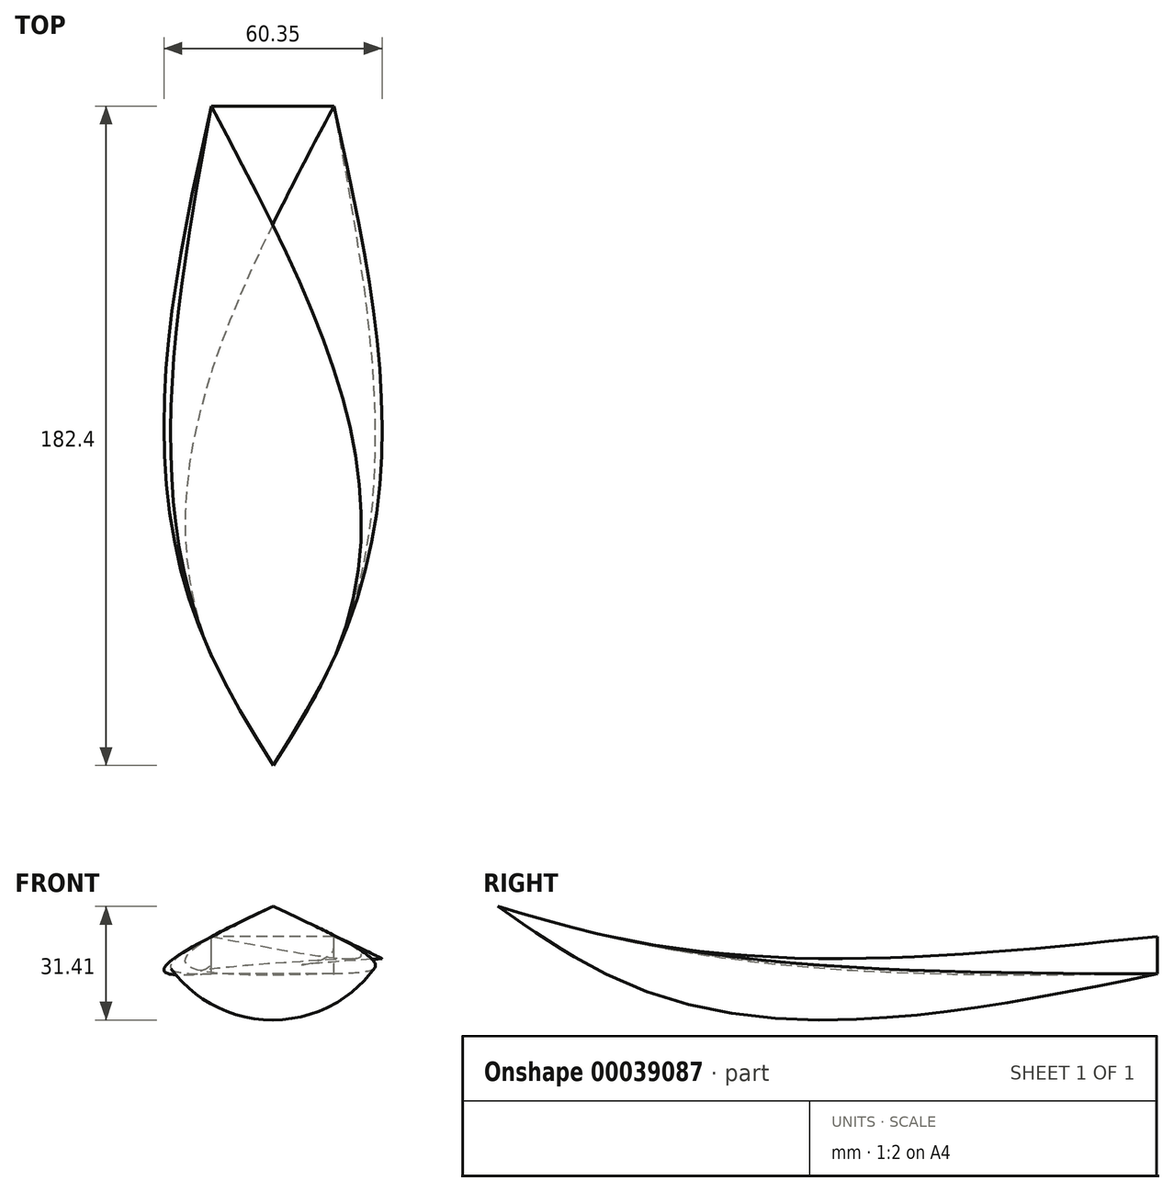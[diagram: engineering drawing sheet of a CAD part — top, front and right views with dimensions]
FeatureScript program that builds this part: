
annotation { "Feature Type Name" : "Feature", "Feature Type Description" : "" }
export const myFeature = defineFeature(function(context is Context, id is Id, definition is map)
    precondition{}
    {
        {
            var Q0;
            Q0=qCreatedBy(makeId("Front.planeOp"),FACE);
            var sketch = newSketch(context, id + "F0", { "sketchPlane" : qUnion([Q0])});
            skLineSegment(sketch, "E0.bottom", {"start": v(46.82, 0) * mm, "end": v(12.91, 0) * mm});
            skLineSegment(sketch, "E0.top", {"start": v(46.82, 10.4) * mm, "end": v(12.91, 10.4) * mm});
            skLineSegment(sketch, "E0.left", {"start": v(46.82, 0) * mm, "end": v(46.82, 10.4) * mm});
            skLineSegment(sketch, "E0.right", {"start": v(12.91, 0) * mm, "end": v(12.91, 10.4) * mm});
            skLineSegment(sketch, "E1.MirrorCS", {"start": v(-12.91, 0) * mm, "end": v(-12.91, 10.4) * mm});
            skLineSegment(sketch, "E2.MirrorCS", {"start": v(-46.82, 0) * mm, "end": v(-46.82, 10.4) * mm});
            skLineSegment(sketch, "E3.MirrorCS", {"start": v(-46.82, 0) * mm, "end": v(-12.91, 0) * mm});
            skLineSegment(sketch, "E4.MirrorCS", {"start": v(-46.82, 10.4) * mm, "end": v(-12.91, 10.4) * mm});
            skSolve(sketch);
        }
        {
            var Q0;
            Q0=qCreatedBy(makeId("Front.planeOp"),FACE);
            cPlane(context, id + "F1", {"entities" : qUnion([Q0]), "cplaneType" : CPlaneType.OFFSET, "offset" : 152.4 * mm, "width" : 152.4 * mm, "height" : 152.4 * mm});
        }
        {
            var Q0;
            Q0=qCreatedBy(id+"F1.planeOp",FACE);
            var sketch = newSketch(context, id + "F2", { "sketchPlane" : qUnion([Q0])});
            skArc(sketch, "E5", {"start": v(-47.02, 10.6) * mm, "mid": v(-30.13, -0.12) * mm, "end": v(-13.12, 10.4) * mm});
            skLineSegment(sketch, "E6", {"start": v(-47.02, 10.6) * mm, "end": v(-13.12, 10.4) * mm});
            skLineSegment(sketch, "E7.MirrorCS", {"start": v(47.02, 10.6) * mm, "end": v(13.12, 10.4) * mm});
            skArc(sketch, "E8.MirrorCS", {"start": v(47.02, 10.6) * mm, "mid": v(30.13, -0.12) * mm, "end": v(13.12, 10.4) * mm});
            skSolve(sketch);
        }
        {
            var Q0;
            Q0=qCreatedBy(id+"F1.planeOp",FACE);
            cPlane(context, id + "F3", {"entities" : qUnion([Q0]), "cplaneType" : CPlaneType.OFFSET, "offset" : 30 * mm, "width" : 150 * mm, "height" : 150 * mm});
        }
        {
            var Q0;
            Q0=qCreatedBy(id+"F3.planeOp",FACE);
            var sketch = newSketch(context, id + "F4", { "sketchPlane" : qUnion([Q0])});
            skPoint(sketch, "E9", {"position": v(-30.07, 18.68) * mm});
            skPoint(sketch, "E10.MirrorP", {"position": v(30.07, 18.68) * mm});
            skSolve(sketch);
        }
        {
            var Q0;
            Q0=makeQuery(id+"F0.imprint","IMPRINT",FACE,{"disambiguationData":[TD([[makeQuery(id+"F0.imprint","IMPRINT",EDGE,{"derivedFrom":sQuery(id+"F0.wireOp",EDGE,"E0.bottom")}),-1.0]])]});
            var Q1;
            Q1=makeQuery(id+"F2.imprint","IMPRINT",FACE,{"disambiguationData":[TD([[makeQuery(id+"F2.imprint","IMPRINT",EDGE,{"derivedFrom":sQuery(id+"F2.wireOp",EDGE,"E7.MirrorCS")}),1.0]])]});
            var Q2;
            Q2=sQuery(id+"F4.wireOp",VERTEX,"E10.MirrorP");
            var Q3;
            Q3=sQuery(id+"F4.wireOp",VERTEX,"E10.MirrorP");
            var Q4;
            Q4=sQuery(id+"F2.wireOp",EDGE,"E8.MirrorCS");
            var Q5;
            Q5=sQuery(id+"F0.wireOp",EDGE,"E0.bottom");
            loft(context, id + "F5", {"bodyType" : ToolBodyType.SURFACE, "sheetProfilesArray" : [{ "sheetProfileEntities" : qUnion([Q0]) }, { "sheetProfileEntities" : qUnion([Q1]) }, { "sheetProfileEntities" : qUnion([Q2]) }], "wireProfilesArray" : [{ "wireProfileEntities" : qUnion([Q3]) }, { "wireProfileEntities" : qUnion([Q4]) }, { "wireProfileEntities" : qUnion([Q5]) }]});
        }
        {
            var Q0;
            Q0=sQuery(id+"F0.wireOp",EDGE,"E0.right");
            var Q1;
            Q1=sQuery(id+"F2.wireOp",EDGE,"E7.MirrorCS");
            var Q2;
            Q2=sQuery(id+"F4.wireOp",VERTEX,"E10.MirrorP");
            loft(context, id + "F6", {"bodyType" : ToolBodyType.SURFACE, "wireProfilesArray" : [{ "wireProfileEntities" : qUnion([Q0]) }, { "wireProfileEntities" : qUnion([Q1]) }, { "wireProfileEntities" : qUnion([Q2]) }]});
        }
        {
            var Q0;
            Q0=sQuery(id+"F0.wireOp",EDGE,"E0.left");
            var Q1;
            Q1=sQuery(id+"F2.wireOp",EDGE,"E7.MirrorCS");
            var Q2;
            Q2=sQuery(id+"F4.wireOp",VERTEX,"E10.MirrorP");
            loft(context, id + "F7", {"bodyType" : ToolBodyType.SURFACE, "wireProfilesArray" : [{ "wireProfileEntities" : qUnion([Q0]) }, { "wireProfileEntities" : qUnion([Q1]) }, { "wireProfileEntities" : qUnion([Q2]) }]});
        }
        {
            var Q0;
            Q0=sQuery(id+"F0.wireOp",EDGE,"E0.left");
            var Q1;
            Q1=sQuery(id+"F0.wireOp",EDGE,"E0.right");
            loft(context, id + "F8", {"bodyType" : ToolBodyType.SURFACE, "wireProfilesArray" : [{ "wireProfileEntities" : qUnion([Q0]) }, { "wireProfileEntities" : qUnion([Q1]) }]});
        }
    });
